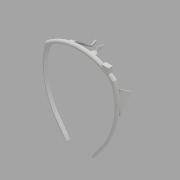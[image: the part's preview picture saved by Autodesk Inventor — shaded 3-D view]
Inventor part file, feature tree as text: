
AUTODESK INVENTOR PART (.ipt)
format: ipt  version: 2017 (Build 210142000, 142)  size: 631,808 bytes
history: native  units: mm
features: other x3, extrude x3, sketch x3, projected_geometry x1
ambient origin geometry x8: Origin, YZ Plane, XZ Plane, XY Plane, X Axis, Y Axis, Z Axis, Center Point
bodies: Solid1 (feature_tree)
feature tree (10):
  other  "pupil_frame.ipt"
  extrude  "Extrusion1"  Depth=12.0mm
  extrude  "Extrusion2"  Depth=12.5mm
  extrude  "Extrusion3"  TaperAngle=60.0deg  [1 undecoded]
  other  "Solid1::pupil_frame.ipt"
  other  "TaggingFeature1"
  sketch  "Sketch12"  dims[d0=10.0mm d1=12.0mm]
  sketch  "Sketch13"  dims[d3=9.0mm d4=12.5mm]
  sketch  "Sketch14"  dims[d5=3.0mm d6=60.0deg d7=10.0mm d8=0.0mm d9=13.5mm d10=41.0mm d11=2.0mm d12=15.53343mm d13=2.0mm d14=21.25mm d15=0.0mm d16=21.25mm d17=0.0mm]
  projected_geometry  "Projected Loop1"
note: 1 required parameter value undecoded (feature->parameter linkage not recoverable at this tier; creation-order binding heuristic only, values carry confidence <= 0.55)
